# Revit family: T200181
name_source: partatom
category: Furniture
revit_build: Autodesk Revit Architecture 2015 (Build: 20140322_1515(x64)
units: mm (PartAtom-declared; Revit-internal decimal feet)

## types (1)
- T200181
    Assembly Code = E2020400
    Catalog = https://ofs.com
    Description = OFS TYPICAL T200181
    Manufacturer = OFS
    Model = T200181
    Staks 15h Shared Organizer Board = OFS STAKS Boards
    Staks 15h Shared Organizer Door = OFS STAKS Doors Material
    Staks Double Sided Frosted Glass = OFS STAKS Frosted Glass
    Staks Spine or Divider Wall = STAKS SURFACE LG
    Staks Support Panel = STAKS SUPPORT WD
    Staks fabric Tackboard = STAKS FABRIC TACKBOARD
    Staks slide Out Storage Tower Chasis = OFS STAKS Veneer Finish
    Staks slide Out Storage Tower Door = OFS STAKS Veneer Finish
    Staks slide Out Storage Tower Door Handle = OFS STAKS Metal Handle Material
    URL = https://ofs.com

## geometry (parser evidence)
native form markers: Blend x96, Sweep x27
no freeform markers — native parametric forms only
